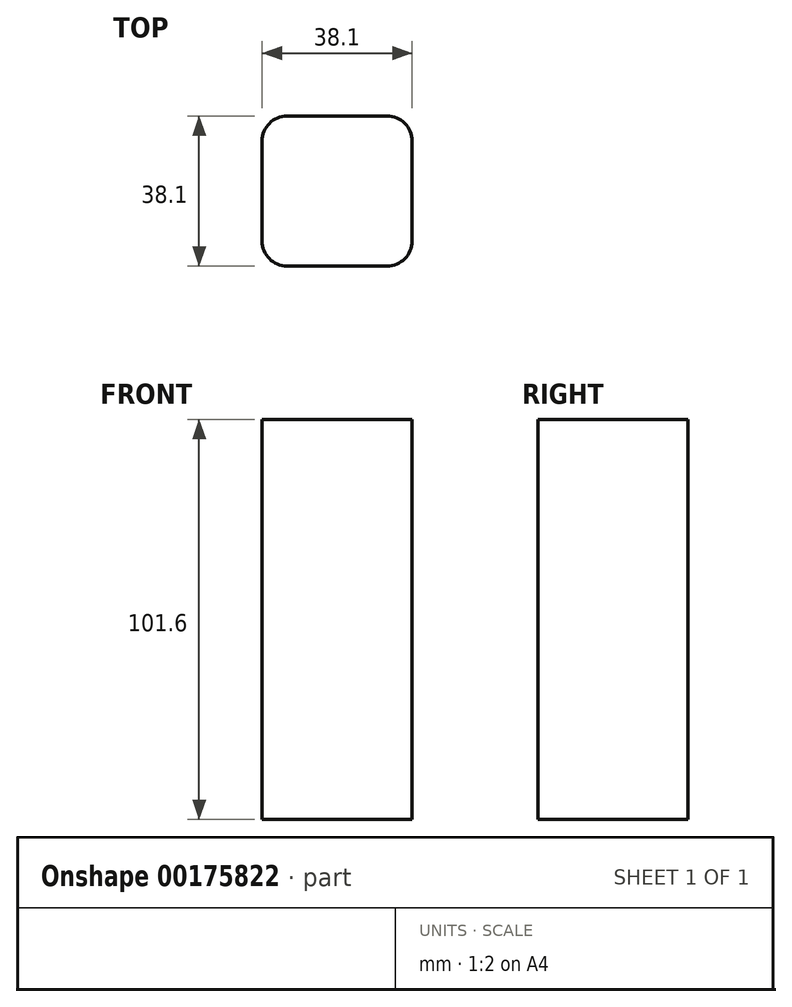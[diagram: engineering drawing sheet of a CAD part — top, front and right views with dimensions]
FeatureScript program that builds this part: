
annotation { "Feature Type Name" : "Feature", "Feature Type Description" : "" }
export const myFeature = defineFeature(function(context is Context, id is Id, definition is map)
    precondition{}
    {
        {
            var Q0;
            Q0=qCreatedBy(makeId("Top.planeOp"),FACE);
            var sketch = newSketch(context, id + "F0", { "sketchPlane" : qUnion([Q0])});
            skLineSegment(sketch, "E0.bottom", {"start": v(12.7, 19.05) * mm, "end": v(-12.7, 19.05) * mm});
            skLineSegment(sketch, "E0.top", {"start": v(12.7, -19.05) * mm, "end": v(-12.7, -19.05) * mm});
            skLineSegment(sketch, "E0.left", {"start": v(19.05, 12.7) * mm, "end": v(19.05, -12.7) * mm});
            skLineSegment(sketch, "E0.right", {"start": v(-19.05, 12.7) * mm, "end": v(-19.05, -12.7) * mm});
            skPoint(sketch, "E0.middle", {"position": v(0, 0) * mm});
            skPoint(sketch, "E1.visualSharp", {"position": v(-19.05, 19.05) * mm});
            skArc(sketch, "E1.filletArc", {"start": v(-12.7, 19.05) * mm, "mid": v(-17.2, 17.2) * mm, "end": v(-19.05, 12.7) * mm});
            skPoint(sketch, "E2.visualSharp", {"position": v(19.05, 19.05) * mm});
            skArc(sketch, "E2.filletArc", {"start": v(19.05, 12.7) * mm, "mid": v(17.2, 17.2) * mm, "end": v(12.7, 19.05) * mm});
            skPoint(sketch, "E3.visualSharp", {"position": v(19.05, -19.05) * mm});
            skArc(sketch, "E3.filletArc", {"start": v(12.7, -19.05) * mm, "mid": v(17.2, -17.2) * mm, "end": v(19.05, -12.7) * mm});
            skPoint(sketch, "E4.visualSharp", {"position": v(-19.05, -19.05) * mm});
            skArc(sketch, "E4.filletArc", {"start": v(-19.05, -12.7) * mm, "mid": v(-17.2, -17.2) * mm, "end": v(-12.7, -19.05) * mm});
            skSolve(sketch);
        }
        {
            var Q0;
            Q0=qSketchRegion(id+"F0",true);
            extrude(context, id + "F1", {"entities" : qUnion([Q0]), "depth" : 101.6 * mm, "offsetDistance" : 25.4 * mm});
        }
    });
